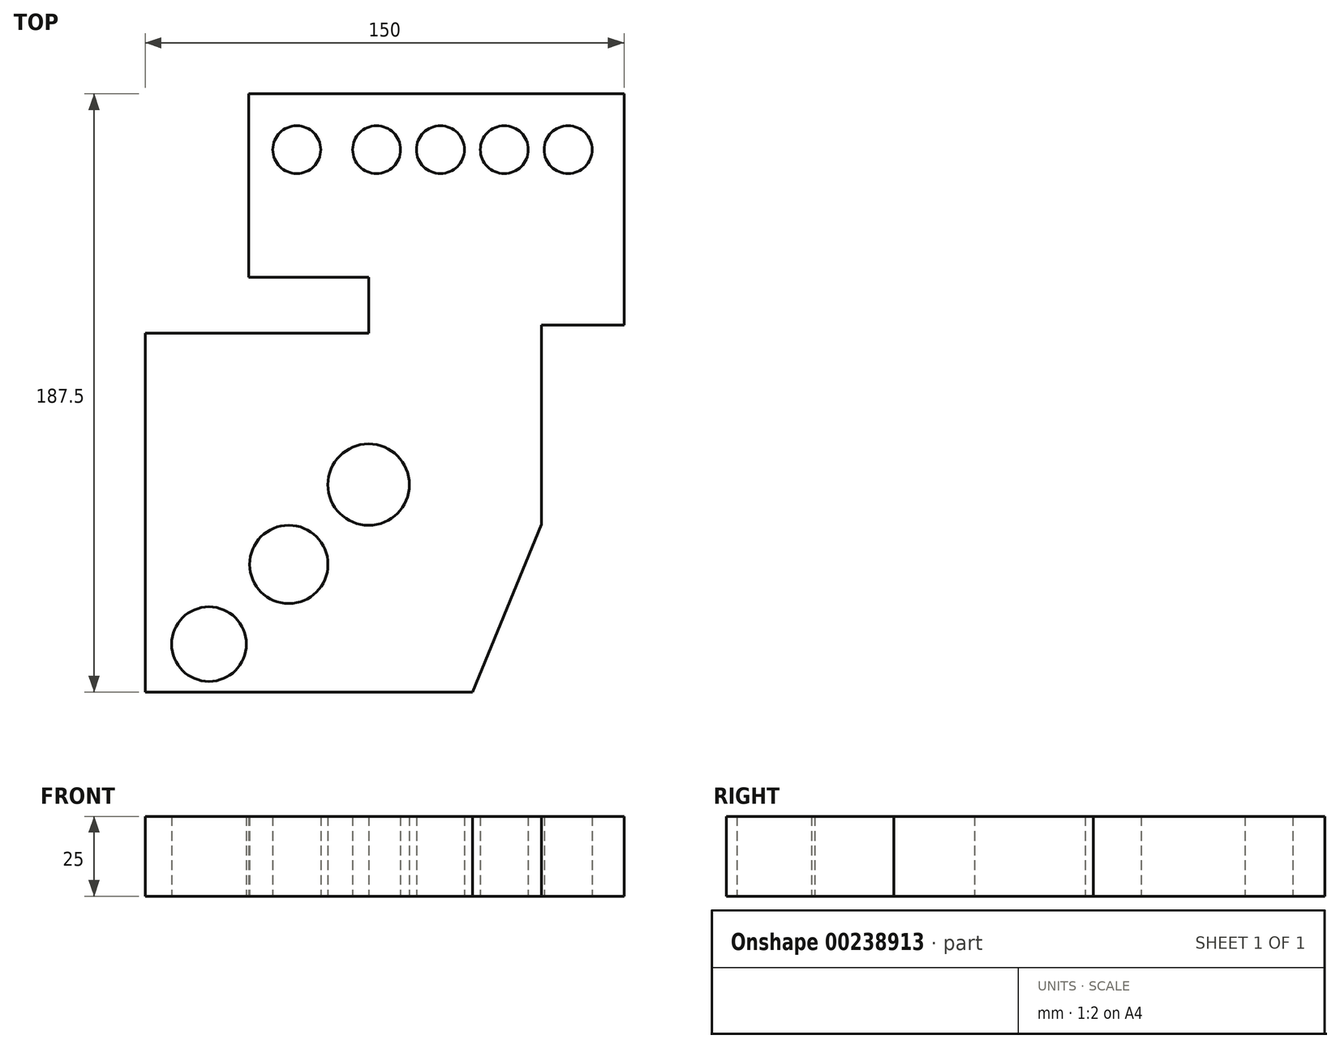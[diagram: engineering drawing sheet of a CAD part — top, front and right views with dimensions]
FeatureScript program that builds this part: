
annotation { "Feature Type Name" : "Feature", "Feature Type Description" : "" }
export const myFeature = defineFeature(function(context is Context, id is Id, definition is map)
    precondition{}
    {
        {
            var Q0;
            Q0=qCreatedBy(makeId("Top.planeOp"),FACE);
            var sketch = newSketch(context, id + "F0", { "sketchPlane" : qUnion([Q0])});
            skLineSegment(sketch, "E0", {"start": v(-70, -55.07) * mm, "end": v(32.5, -55.07) * mm});
            skLineSegment(sketch, "E1", {"start": v(32.5, -55.07) * mm, "end": v(54.18, -2.57) * mm});
            skLineSegment(sketch, "E2", {"start": v(54.18, 59.93) * mm, "end": v(54.18, -2.57) * mm});
            skLineSegment(sketch, "E3", {"start": v(54.18, 59.93) * mm, "end": v(80, 59.93) * mm});
            skLineSegment(sketch, "E4", {"start": v(80, 132.43) * mm, "end": v(80, 59.93) * mm});
            skLineSegment(sketch, "E5", {"start": v(80, 132.43) * mm, "end": v(-37.5, 132.43) * mm});
            skLineSegment(sketch, "E6", {"start": v(-37.5, 132.43) * mm, "end": v(-37.5, 74.93) * mm});
            skLineSegment(sketch, "E7", {"start": v(-37.5, 74.93) * mm, "end": v(0, 74.93) * mm});
            skLineSegment(sketch, "E8", {"start": v(0, 74.93) * mm, "end": v(0, 57.43) * mm});
            skLineSegment(sketch, "E9", {"start": v(0, 57.43) * mm, "end": v(-70, 57.43) * mm});
            skLineSegment(sketch, "E10", {"start": v(-70, 57.43) * mm, "end": v(-70, -55.07) * mm});
            skCircle(sketch, "E11", {"center": v(-50, -40.07) * mm, "radius": 11.7 * mm});
            skCircle(sketch, "E12", {"center": v(-25, -15.07) * mm, "radius": 12.27 * mm});
            skCircle(sketch, "E13", {"center": v(0, 9.93) * mm, "radius": 12.76 * mm});
            skCircle(sketch, "E14", {"center": v(-22.5, 114.93) * mm, "radius": 7.5 * mm});
            skCircle(sketch, "E15", {"center": v(2.5, 114.93) * mm, "radius": 7.5 * mm});
            skCircle(sketch, "E16", {"center": v(22.5, 114.93) * mm, "radius": 7.5 * mm});
            skCircle(sketch, "E17", {"center": v(42.5, 114.93) * mm, "radius": 7.5 * mm});
            skCircle(sketch, "E18", {"center": v(62.5, 114.93) * mm, "radius": 7.5 * mm});
            skSolve(sketch);
        }
        {
            var Q0;
            Q0 = qSketchRegion(id + "F0", true);
            extrude(context, id + "F1", {"entities" : qUnion([Q0]), "depth" : 25 * mm});
        }
    });
